# Revit family: Kabelrinnen-Systeme_begehbar_Kabelrinne_BRKS
name_source: partatom
category: Generic Models
revit_build: Autodesk Revit 2015 (Build: 20140606_1530(x64)
units: mm (PartAtom-declared; Revit-internal decimal feet)

## types (12) — shared parameters
Manufacturer = OBO Bettermann
Material = Steel, Galvanized
URL = http://www.obo-bettermann.com

## per-type parameters (varying)
| type | "B" Dimension | GTIN | H | Manufacturer Art. No. |
| BKRS 1030 FS | 300 mm | 4012196341887 | 98 mm  [stored 0.321522 ft] | 6062004 |
| BKRS 1020 FS | 200 mm  [stored 0.656168 ft] | 4012196341870 | 98 mm  [stored 0.321522 ft] | 6062002 |
| BKRS 1010 FS | 100 mm  [stored 0.328084 ft] | 4012196341863 | 98 mm  [stored 0.321522 ft] | 6062000 |
| BKRS 1040 FS | 400 mm  [stored 1.31234 ft] | 4012196341894 | 98 mm  [stored 0.321522 ft] | 6062006 |
| BKRS 1060 FS | 600 mm | 4012196341917 | 98 mm  [stored 0.321522 ft] | 6062010 |
| BKRS 1120 FS | 200 mm  [stored 0.656168 ft] | 4012196147038 | 107 mm  [stored 0.35105 ft] | 6061983 |
| BKRS 1140 FS | 400 mm  [stored 1.31234 ft] | 4012196147052 | 107 mm  [stored 0.35105 ft] | 6061987 |
| BKRS 1160 FS | 600 mm | 4012196147090 | 107 mm  [stored 0.35105 ft] | 6061991 |
| BKRS 1050 FS | 500 mm  [stored 1.64042 ft] | 4012196341900 | 98 mm  [stored 0.321522 ft] | 6062008 |
| BKRS 1110 FS | 100 mm  [stored 0.328084 ft] | 4012196147007 | 107 mm  [stored 0.35105 ft] | 6061981 |
| BKRS 1130 FS | 300 mm | 4012196147045 | 107 mm  [stored 0.35105 ft] | 6061985 |
| BKRS 1150 FS | 500 mm  [stored 1.64042 ft] | 4012196147069 | 107 mm  [stored 0.35105 ft] | 6061989 |

note: column(s) folded — value = type name in every type: Article Type

note: [stored X ft] marks values corroborated as IEEE doubles in the binary element streams (Revit-internal decimal feet)

## geometry (parser evidence)
native form markers: Sweep x2
no freeform markers — native parametric forms only
